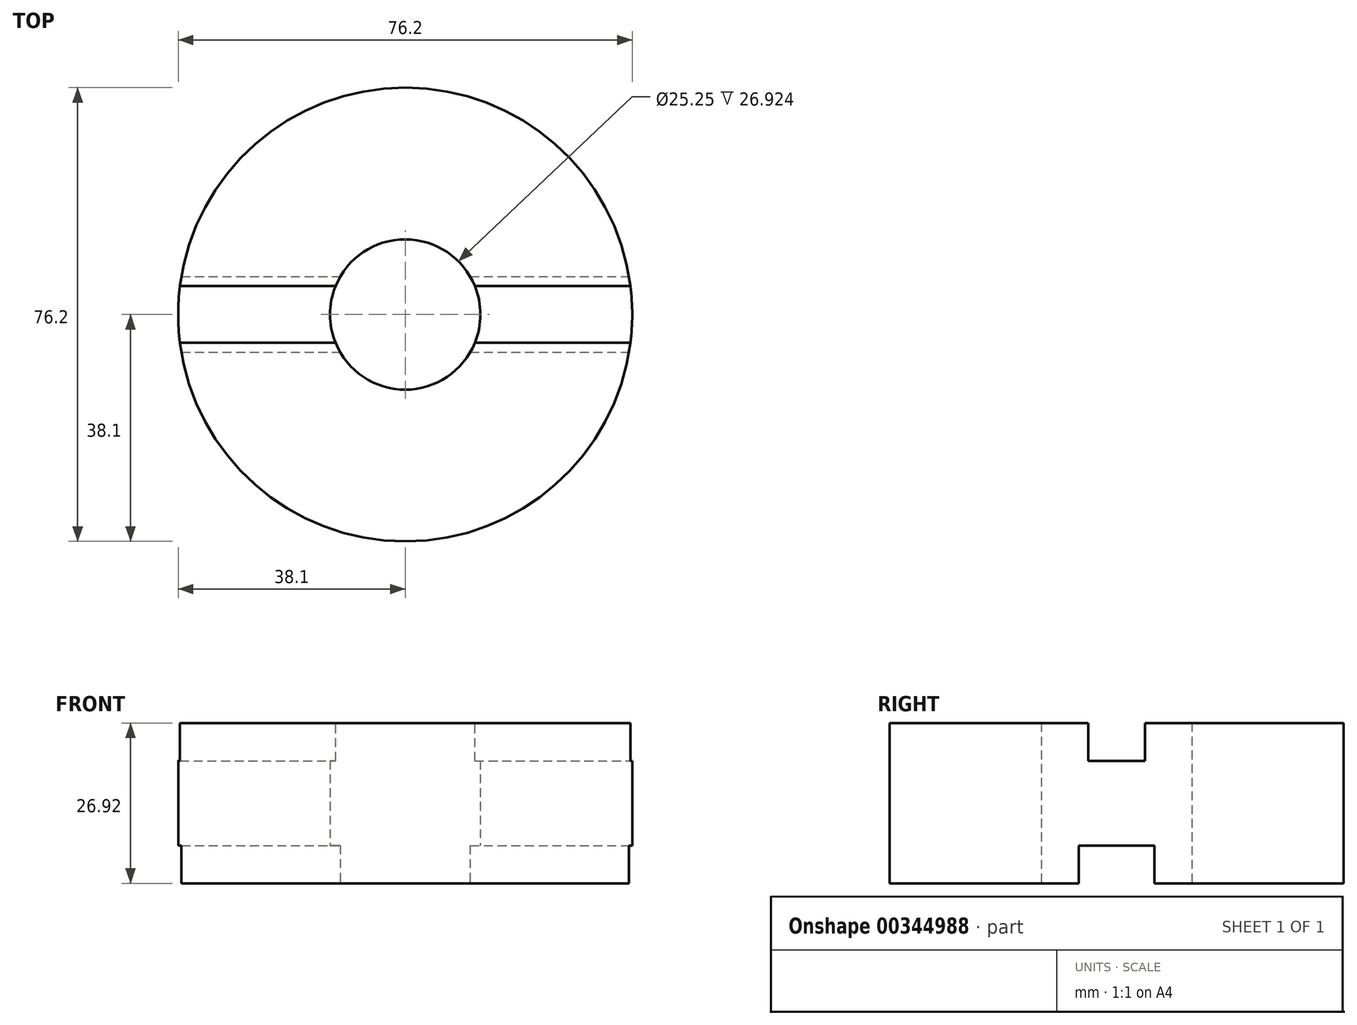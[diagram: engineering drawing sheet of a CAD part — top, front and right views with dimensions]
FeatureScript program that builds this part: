
annotation { "Feature Type Name" : "Feature", "Feature Type Description" : "" }
export const myFeature = defineFeature(function(context is Context, id is Id, definition is map)
    precondition{}
    {
        {
            var Q0;
            Q0=qCreatedBy(makeId("Top.planeOp"),FACE);
            var sketch = newSketch(context, id + "F0", { "sketchPlane" : qUnion([Q0])});
            skCircle(sketch, "E0", {"center": v(0, 0) * mm, "radius": 38.1 * mm});
            skCircle(sketch, "E1", {"center": v(0, 0) * mm, "radius": 12.62 * mm});
            skSolve(sketch);
        }
        {
            var Q0;
            Q0=makeQuery(id+"F0.imprint","IMPRINT",FACE,{"disambiguationData":[TD([[makeQuery(id+"F0.imprint","IMPRINT",EDGE,{"derivedFrom":sQuery(id+"F0.wireOp",EDGE,"E0")}),1.0]])]});
            extrude(context, id + "F1", {"entities" : qUnion([Q0]), "depth" : 26.92 * mm});
        }
        {
            var Q0;
            Q0=makeQuery(id+"F1.opExtrude","CAP_FACE",FACE,{"disambiguationData":[OSD([sQuery(id+"F0.wireOp",EDGE,"E0"),sQuery(id+"F0.wireOp",EDGE,"E1")])],"isStart":false});
            var sketch = newSketch(context, id + "F2", { "sketchPlane" : qUnion([Q0])});
            skLineSegment(sketch, "E2.bottom", {"start": v(-38.1, 4.76) * mm, "end": v(38.1, 4.76) * mm});
            skLineSegment(sketch, "E2.top", {"start": v(-38.1, -4.76) * mm, "end": v(38.1, -4.76) * mm});
            skLineSegment(sketch, "E2.left", {"start": v(-38.1, 4.76) * mm, "end": v(-38.1, -4.76) * mm});
            skLineSegment(sketch, "E2.right", {"start": v(38.1, 4.76) * mm, "end": v(38.1, -4.76) * mm});
            skLineSegment(sketch, "E3", {"start": v(0, 4.76) * mm, "end": v(0, -4.76) * mm, "construction": true});
            skLineSegment(sketch, "E4", {"start": v(38.1, 0) * mm, "end": v(-38.1, 0) * mm, "construction": true});
            skSolve(sketch);
        }
        {
            var Q0;
            {var subQ1=makeQuery(id+"F1.opExtrude","CAP_EDGE",EDGE,{"disambiguationData":[OSD([sQuery(id+"F0.wireOp",EDGE,"E0")])],"isStart":false});var subQ4=sQuery(id+"F2.wireOp",EDGE,"E2.bottom");var subQ5=makeQuery(id+"F2.imprint","INTERSECT",VERTEX,{"disambiguationData":[OD(0.0)],"derivedFrom":[subQ1,subQ4]});Q0=makeQuery(id+"F2.imprint","IMPRINT",FACE,{"disambiguationData":[TD([[makeQuery(id+"F2.imprint","IMPRINT",EDGE,{"disambiguationData":[TD([[subQ5,-1.0]])],"derivedFrom":subQ4}),-1.0]])]});}
            var Q1;
            {var subQ1=makeQuery(id+"F1.opExtrude","CAP_EDGE",EDGE,{"disambiguationData":[OSD([sQuery(id+"F0.wireOp",EDGE,"E0")])],"isStart":false});var subQ6=sQuery(id+"F2.wireOp",EDGE,"E2.bottom");var subQ7=makeQuery(id+"F2.imprint","INTERSECT",VERTEX,{"disambiguationData":[OD(1.0)],"derivedFrom":[subQ1,subQ6]});Q1=makeQuery(id+"F2.imprint","IMPRINT",FACE,{"disambiguationData":[TD([[makeQuery(id+"F2.imprint","IMPRINT",EDGE,{"disambiguationData":[TD([[subQ7,1.0]])],"derivedFrom":subQ6}),-1.0]])]});}
            extrude(context, id + "F3", {"entities" : qUnion([Q0, Q1]), "operationType" : NewBodyOperationType.REMOVE, "oppositeDirection" : true, "depth" : 6.35 * mm});
        }
        {
            var Q0;
            Q0=makeQuery(id+"F1.opExtrude","CAP_FACE",FACE,{"disambiguationData":[OSD([sQuery(id+"F0.wireOp",EDGE,"E0"),sQuery(id+"F0.wireOp",EDGE,"E1")])],"isStart":true});
            var sketch = newSketch(context, id + "F4", { "sketchPlane" : qUnion([Q0])});
            skLineSegment(sketch, "E5.bottom", {"start": v(-38.1, 6.35) * mm, "end": v(38.1, 6.35) * mm});
            skLineSegment(sketch, "E5.top", {"start": v(-38.1, -6.35) * mm, "end": v(38.1, -6.35) * mm});
            skLineSegment(sketch, "E5.left", {"start": v(-38.1, 6.35) * mm, "end": v(-38.1, -6.35) * mm});
            skLineSegment(sketch, "E5.right", {"start": v(38.1, 6.35) * mm, "end": v(38.1, -6.35) * mm});
            skLineSegment(sketch, "E6", {"start": v(-38.1, 0) * mm, "end": v(38.1, 0) * mm, "construction": true});
            skLineSegment(sketch, "E7", {"start": v(0, 6.35) * mm, "end": v(0, -6.35) * mm, "construction": true});
            skSolve(sketch);
        }
        {
            var Q0;
            {var subQ1=makeQuery(id+"F1.opExtrude","CAP_EDGE",EDGE,{"disambiguationData":[OSD([sQuery(id+"F0.wireOp",EDGE,"E0")])],"isStart":true});var subQ4=sQuery(id+"F4.wireOp",EDGE,"E5.bottom");var subQ5=makeQuery(id+"F4.imprint","INTERSECT",VERTEX,{"disambiguationData":[OD(0.0)],"derivedFrom":[subQ1,subQ4]});Q0=makeQuery(id+"F4.imprint","IMPRINT",FACE,{"disambiguationData":[TD([[makeQuery(id+"F4.imprint","IMPRINT",EDGE,{"disambiguationData":[TD([[subQ5,-1.0]])],"derivedFrom":subQ4}),-1.0]])]});}
            var Q1;
            {var subQ1=makeQuery(id+"F1.opExtrude","CAP_EDGE",EDGE,{"disambiguationData":[OSD([sQuery(id+"F0.wireOp",EDGE,"E0")])],"isStart":true});var subQ6=sQuery(id+"F4.wireOp",EDGE,"E5.bottom");var subQ7=makeQuery(id+"F4.imprint","INTERSECT",VERTEX,{"disambiguationData":[OD(1.0)],"derivedFrom":[subQ1,subQ6]});Q1=makeQuery(id+"F4.imprint","IMPRINT",FACE,{"disambiguationData":[TD([[makeQuery(id+"F4.imprint","IMPRINT",EDGE,{"disambiguationData":[TD([[subQ7,1.0]])],"derivedFrom":subQ6}),-1.0]])]});}
            extrude(context, id + "F5", {"entities" : qUnion([Q0, Q1]), "operationType" : NewBodyOperationType.REMOVE, "oppositeDirection" : true, "depth" : 6.35 * mm});
        }
    });
